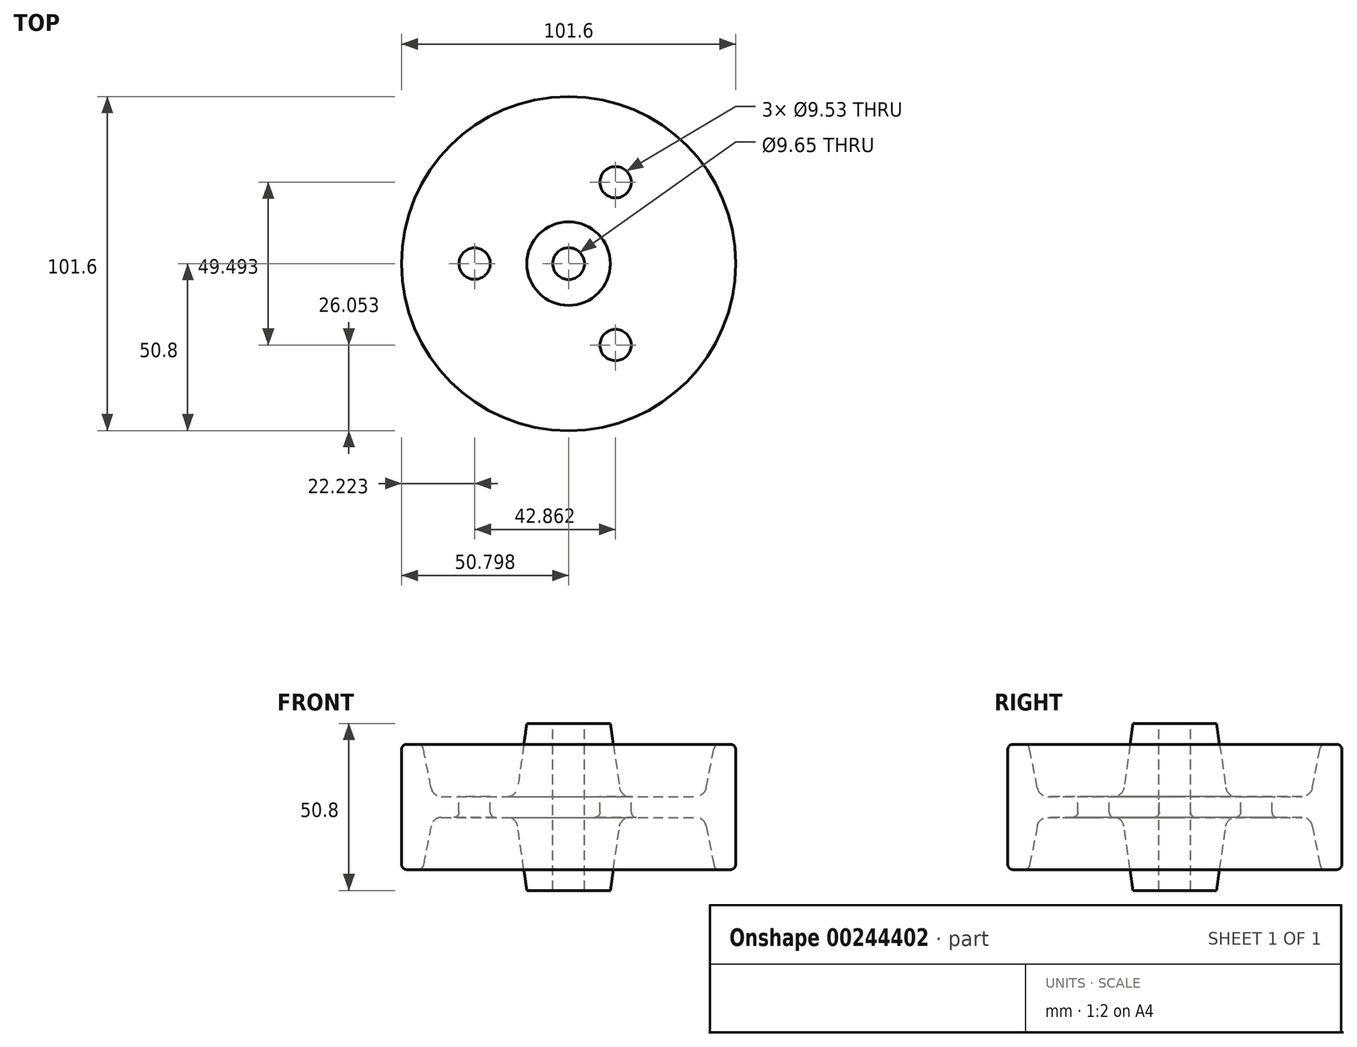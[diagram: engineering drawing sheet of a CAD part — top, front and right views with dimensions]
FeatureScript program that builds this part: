
annotation { "Feature Type Name" : "Feature", "Feature Type Description" : "" }
export const myFeature = defineFeature(function(context is Context, id is Id, definition is map)
    precondition{}
    {
        {
            var Q0;
            Q0=qCreatedBy(makeId("Front.planeOp"),FACE);
            var sketch = newSketch(context, id + "F0", { "sketchPlane" : qUnion([Q0])});
            skLineSegment(sketch, "E0", {"start": v(-50.2, 4.3) * mm, "end": v(-50.2, -33.8) * mm});
            skLineSegment(sketch, "E1", {"start": v(-50.2, -14.75) * mm, "end": v(0.6, -14.75) * mm});
            skLineSegment(sketch, "E2", {"start": v(-50.2, -14.75) * mm, "end": v(-40.68, -14.75) * mm});
            skLineSegment(sketch, "E3", {"start": v(-50.2, -33.8) * mm, "end": v(-43.85, -33.8) * mm});
            skLineSegment(sketch, "E4", {"start": v(-43.85, -33.8) * mm, "end": v(-41.19, -20.48) * mm});
            skLineSegment(sketch, "E5", {"start": v(0.6, -14.75) * mm, "end": v(0.6, -40.15) * mm});
            skLineSegment(sketch, "E6", {"start": v(0.6, -40.15) * mm, "end": v(-12.1, -40.15) * mm});
            skLineSegment(sketch, "E7", {"start": v(-38.07, -17.93) * mm, "end": v(-18.03, -17.93) * mm});
            skLineSegment(sketch, "E8", {"start": v(0.6, -14.75) * mm, "end": v(-15.28, -14.75) * mm});
            skLineSegment(sketch, "E9", {"start": v(-14.89, -20.65) * mm, "end": v(-12.1, -40.15) * mm});
            skPoint(sketch, "E10.visualSharp", {"position": v(-40.68, -17.93) * mm});
            skArc(sketch, "E10.filletArc", {"start": v(-38.07, -17.93) * mm, "mid": v(-40.09, -18.65) * mm, "end": v(-41.19, -20.48) * mm});
            skPoint(sketch, "E11.visualSharp", {"position": v(-15.28, -17.93) * mm});
            skArc(sketch, "E11.filletArc", {"start": v(-14.89, -20.65) * mm, "mid": v(-15.95, -18.7) * mm, "end": v(-18.03, -17.93) * mm});
            skLineSegment(sketch, "E12.MirrorCS", {"start": v(-38.07, -11.58) * mm, "end": v(-18.03, -11.58) * mm});
            skArc(sketch, "E13.MirrorCS", {"start": v(-14.89, -8.85) * mm, "mid": v(-15.95, -10.8) * mm, "end": v(-18.03, -11.58) * mm});
            skLineSegment(sketch, "E14.MirrorCS", {"start": v(-14.89, -8.85) * mm, "end": v(-12.1, 10.65) * mm});
            skLineSegment(sketch, "E15.MirrorCS", {"start": v(0.6, 10.65) * mm, "end": v(-12.1, 10.65) * mm});
            skLineSegment(sketch, "E16.MirrorCS", {"start": v(0.6, -14.75) * mm, "end": v(0.6, 10.65) * mm});
            skArc(sketch, "E17.MirrorCS", {"start": v(-38.07, -11.58) * mm, "mid": v(-40.09, -10.86) * mm, "end": v(-41.19, -9.02) * mm});
            skLineSegment(sketch, "E18.MirrorCS", {"start": v(-43.85, 4.3) * mm, "end": v(-41.19, -9.02) * mm});
            skLineSegment(sketch, "E19.MirrorCS", {"start": v(-50.2, 4.3) * mm, "end": v(-43.85, 4.3) * mm});
            skSolve(sketch);
        }
        {
            var Q0;
            Q0=makeQuery(id+"F0.imprint","IMPRINT",FACE,{"disambiguationData":[TD([[makeQuery(id+"F0.imprint","IMPRINT",EDGE,{"derivedFrom":sQuery(id+"F0.wireOp",EDGE,"E12.MirrorCS")}),-1.0]])]});
            var Q1;
            {var subQ11=sQuery(id+"F0.wireOp",EDGE,"E3");Q1=qUnion([makeQuery(id+"F0.imprint","IMPRINT",FACE,{"disambiguationData":[TD([[makeQuery(id+"F0.imprint","IMPRINT",EDGE,{"derivedFrom":subQ11}),1.0]])]}),makeQuery(id+"F0.imprint","IMPRINT",FACE,{"disambiguationData":[TD([[makeQuery(id+"F0.imprint","IMPRINT",EDGE,{"derivedFrom":sQuery(id+"F0.wireOp",EDGE,"E12.MirrorCS")}),-1.0]])]})]);}
            var Q2;
            Q2=sQuery(id+"F0.wireOp",EDGE,"E16.MirrorCS");
            revolve(context, id + "F1", {"entities" : qUnion([Q0, Q1]), "axis" : qUnion([Q2]), "revolveType" : RevolveType.FULL});
        }
        {
            var Q0;
            Q0=makeQuery(id+"F1.opRevolve","SWEPT_FACE",FACE,{"disambiguationData":[OSD([sQuery(id+"F0.wireOp",EDGE,"E15.MirrorCS")])]});
            var sketch = newSketch(context, id + "F2", { "sketchPlane" : qUnion([Q0])});
            skCircle(sketch, "E20", {"center": v(0.6, 0) * mm, "radius": 4.83 * mm});
            skSolve(sketch);
        }
        {
            var Q0;
            Q0=makeQuery(id+"F2.imprint","IMPRINT",FACE,{"disambiguationData":[TD([[makeQuery(id+"F2.imprint","IMPRINT",EDGE,{"derivedFrom":sQuery(id+"F2.wireOp",EDGE,"E20")}),1.0]])]});
            var Q1;
            Q1=sQuery(id+"F2.wireOp",EDGE,"E20");
            extrude(context, id + "F3", {"entities" : qUnion([Q0]), "operationType" : NewBodyOperationType.REMOVE, "surfaceEntities" : qUnion([Q1]), "endBound" : BoundingType.THROUGH_ALL, "oppositeDirection" : true, "depth" : 25.4 * mm});
        }
        {
            var Q0;
            Q0=makeQuery(id+"F1.opRevolve","SWEPT_FACE",FACE,{"disambiguationData":[OSD([sQuery(id+"F0.wireOp",EDGE,"E12.MirrorCS")])]});
            var sketch = newSketch(context, id + "F4", { "sketchPlane" : qUnion([Q0])});
            skCircle(sketch, "E21", {"center": v(-27.98, 0) * mm, "radius": 4.76 * mm});
            skCircle(sketch, "E22.1.0", {"center": v(14.89, -24.75) * mm, "radius": 4.76 * mm});
            skCircle(sketch, "E22.2.0", {"center": v(14.89, 24.75) * mm, "radius": 4.76 * mm});
            skPoint(sketch, "E22.center", {"position": v(0.6, 0) * mm});
            skSolve(sketch);
        }
        {
            var Q0;
            Q0=makeQuery(id+"F4.imprint","IMPRINT",FACE,{"disambiguationData":[TD([[makeQuery(id+"F4.imprint","IMPRINT",EDGE,{"derivedFrom":sQuery(id+"F4.wireOp",EDGE,"E21")}),1.0]])]});
            var Q1;
            Q1=makeQuery(id+"F4.imprint","IMPRINT",FACE,{"disambiguationData":[TD([[makeQuery(id+"F4.imprint","IMPRINT",EDGE,{"derivedFrom":sQuery(id+"F4.wireOp",EDGE,"E22.2.0")}),1.0]])]});
            var Q2;
            Q2=makeQuery(id+"F4.imprint","IMPRINT",FACE,{"disambiguationData":[TD([[makeQuery(id+"F4.imprint","IMPRINT",EDGE,{"derivedFrom":sQuery(id+"F4.wireOp",EDGE,"E22.1.0")}),1.0]])]});
            extrude(context, id + "F5", {"entities" : qUnion([Q0, Q1, Q2]), "operationType" : NewBodyOperationType.REMOVE, "endBound" : BoundingType.THROUGH_ALL, "oppositeDirection" : true, "depth" : 25.4 * mm});
        }
        {
            var Q0;
            Q0=makeQuery(id+"F1.opRevolve","SWEPT_EDGE",EDGE,{"disambiguationData":[OSD([sQuery(id+"F0.wireOp",EDGE,"E0"),sQuery(id+"F0.wireOp",EDGE,"E19.MirrorCS")])]});
            var Q1;
            Q1=makeQuery(id+"F1.opRevolve","SWEPT_EDGE",EDGE,{"disambiguationData":[OSD([sQuery(id+"F0.wireOp",EDGE,"E0"),sQuery(id+"F0.wireOp",EDGE,"E3")])]});
            var Q2;
            Q2=makeQuery(id+"F1.opRevolve","SWEPT_EDGE",EDGE,{"disambiguationData":[OSD([sQuery(id+"F0.wireOp",EDGE,"E3"),sQuery(id+"F0.wireOp",EDGE,"E4")])]});
            var Q3;
            Q3=makeQuery(id+"F1.opRevolve","SWEPT_EDGE",EDGE,{"disambiguationData":[OSD([sQuery(id+"F0.wireOp",EDGE,"E18.MirrorCS"),sQuery(id+"F0.wireOp",EDGE,"E19.MirrorCS")])]});
            fillet(context, id + "F6", {"entities" : qUnion([Q0, Q1, Q2, Q3]), "radius" : 1.59 * mm, "tangentPropagation" : true, "allowEdgeOverflow" : false});
        }
        {
            var Q0;
            Q0=makeQuery(id+"F5.boolean.opBoolean","COPY",EDGE,{"derivedFrom":makeQuery(id+"F5.opExtrude","CAP_EDGE",EDGE,{"disambiguationData":[OSD([sQuery(id+"F4.wireOp",EDGE,"E22.2.0")])],"isStart":true})});
            var Q1;
            Q1=makeQuery(id+"F5.boolean.opBoolean","COPY",EDGE,{"derivedFrom":makeQuery(id+"F5.opExtrude","CAP_EDGE",EDGE,{"disambiguationData":[OSD([sQuery(id+"F4.wireOp",EDGE,"E22.1.0")])],"isStart":true})});
            var Q2;
            Q2=makeQuery(id+"F5.boolean.opBoolean","INTERSECT",EDGE,{"derivedFrom":[makeQuery(id+"F1.opRevolve","SWEPT_FACE",FACE,{"disambiguationData":[OSD([sQuery(id+"F0.wireOp",EDGE,"E7")])]}),makeQuery(id+"F5.opExtrude","SWEPT_FACE",FACE,{"disambiguationData":[OSD([sQuery(id+"F4.wireOp",EDGE,"E21")])]})]});
            var Q3;
            Q3=makeQuery(id+"F5.boolean.opBoolean","INTERSECT",EDGE,{"derivedFrom":[makeQuery(id+"F1.opRevolve","SWEPT_FACE",FACE,{"disambiguationData":[OSD([sQuery(id+"F0.wireOp",EDGE,"E7")])]}),makeQuery(id+"F5.opExtrude","SWEPT_FACE",FACE,{"disambiguationData":[OSD([sQuery(id+"F4.wireOp",EDGE,"E22.1.0")])]})]});
            var Q4;
            Q4=makeQuery(id+"F5.boolean.opBoolean","INTERSECT",EDGE,{"derivedFrom":[makeQuery(id+"F1.opRevolve","SWEPT_FACE",FACE,{"disambiguationData":[OSD([sQuery(id+"F0.wireOp",EDGE,"E7")])]}),makeQuery(id+"F5.opExtrude","SWEPT_FACE",FACE,{"disambiguationData":[OSD([sQuery(id+"F4.wireOp",EDGE,"E22.2.0")])]})]});
            var Q5;
            Q5=makeQuery(id+"F5.boolean.opBoolean","COPY",EDGE,{"derivedFrom":makeQuery(id+"F5.opExtrude","CAP_EDGE",EDGE,{"disambiguationData":[OSD([sQuery(id+"F4.wireOp",EDGE,"E21")])],"isStart":true})});
            fillet(context, id + "F7", {"entities" : qUnion([Q0, Q1, Q2, Q3, Q4, Q5]), "radius" : 1.59 * mm, "tangentPropagation" : true, "allowEdgeOverflow" : false});
        }
    });
